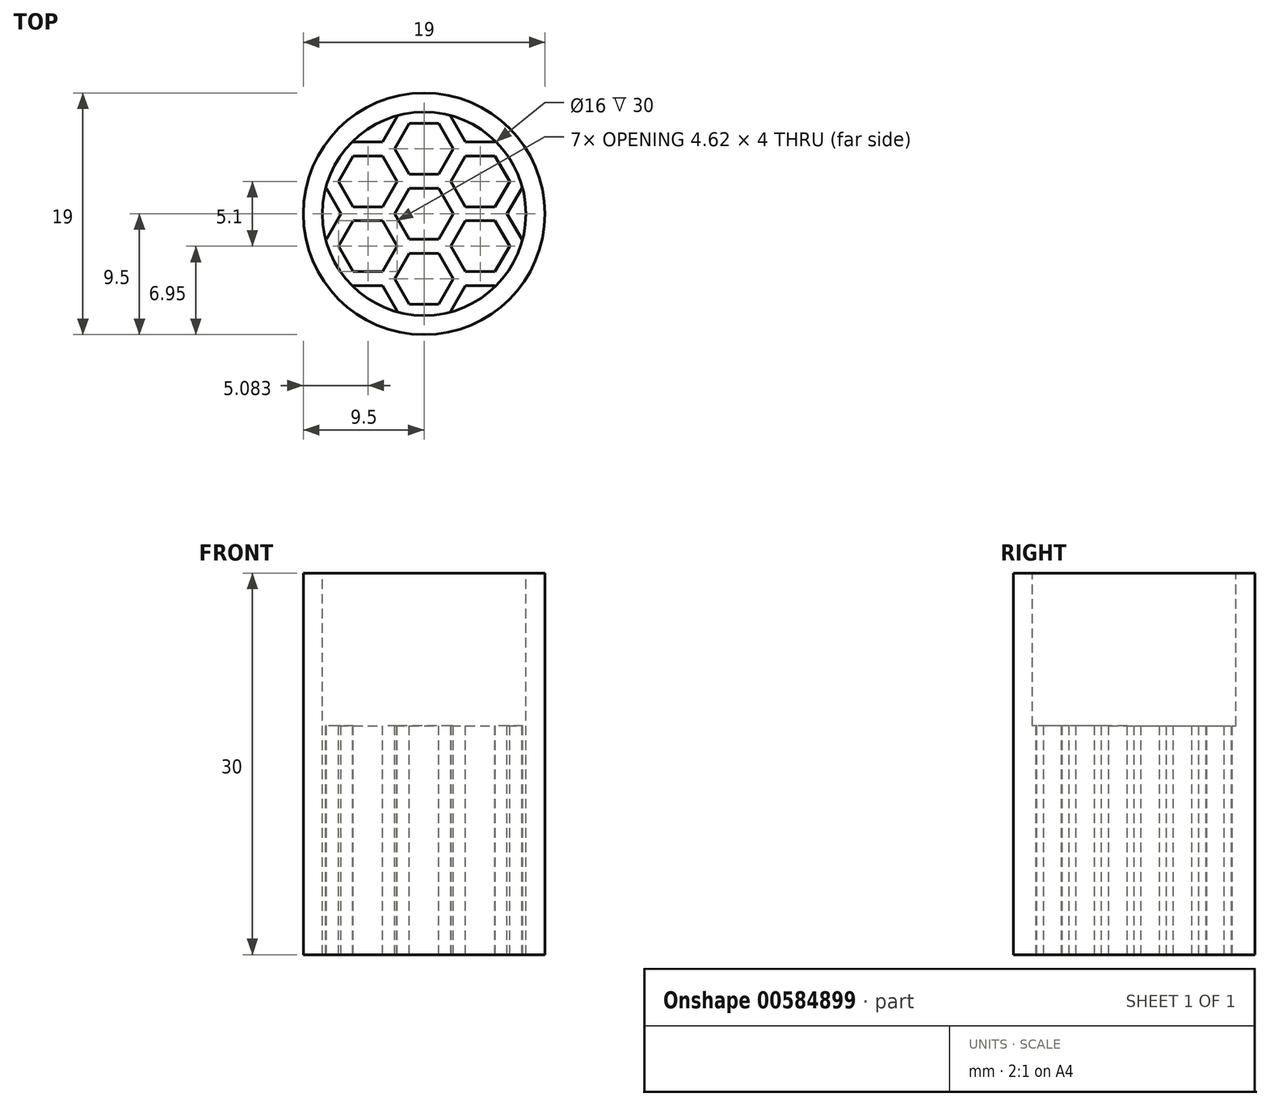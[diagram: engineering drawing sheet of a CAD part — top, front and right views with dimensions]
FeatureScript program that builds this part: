
annotation { "Feature Type Name" : "Feature", "Feature Type Description" : "" }
export const myFeature = defineFeature(function(context is Context, id is Id, definition is map)
    precondition{}
    {
        {
            var Q0;
            Q0=qCreatedBy(makeId("Top.planeOp"),FACE);
            var sketch = newSketch(context, id + "F0", { "sketchPlane" : qUnion([Q0])});
            skCircle(sketch, "E0", {"center": v(0, 0) * mm, "radius": 9.5 * mm});
            skCircle(sketch, "E1", {"center": v(0, 0) * mm, "radius": 8 * mm});
            skCircle(sketch, "E2.cCircle", {"center": v(-10.76, 15.35) * mm, "radius": 2 * mm, "construction": true});
            skLineSegment(sketch, "E2.0", {"start": v(-8.45, 15.35) * mm, "end": v(-9.6, 13.35) * mm});
            skLineSegment(sketch, "E2.1", {"start": v(-9.6, 13.35) * mm, "end": v(-11.91, 13.35) * mm});
            skLineSegment(sketch, "E2.2", {"start": v(-11.91, 13.35) * mm, "end": v(-13.07, 15.35) * mm});
            skLineSegment(sketch, "E2.3", {"start": v(-13.07, 15.35) * mm, "end": v(-11.91, 17.35) * mm});
            skLineSegment(sketch, "E2.4", {"start": v(-11.91, 17.35) * mm, "end": v(-9.6, 17.35) * mm});
            skLineSegment(sketch, "E2.5", {"start": v(-9.6, 17.35) * mm, "end": v(-8.45, 15.35) * mm});
            skPoint(sketch, "E2.0.midPoint", {"position": v(-9.02, 14.35) * mm});
            skCircle(sketch, "E3.cCircle", {"center": v(-10.76, 15.35) * mm, "radius": 2.55 * mm, "construction": true});
            skLineSegment(sketch, "E3.0", {"start": v(-7.81, 15.35) * mm, "end": v(-9.28, 12.8) * mm});
            skLineSegment(sketch, "E3.1", {"start": v(-9.28, 12.8) * mm, "end": v(-12.23, 12.8) * mm});
            skLineSegment(sketch, "E3.2", {"start": v(-12.23, 12.8) * mm, "end": v(-13.7, 15.35) * mm});
            skLineSegment(sketch, "E3.3", {"start": v(-13.7, 15.35) * mm, "end": v(-12.23, 17.9) * mm});
            skLineSegment(sketch, "E3.4", {"start": v(-12.23, 17.9) * mm, "end": v(-9.28, 17.9) * mm});
            skLineSegment(sketch, "E3.5", {"start": v(-9.28, 17.9) * mm, "end": v(-7.81, 15.35) * mm});
            skPoint(sketch, "E3.0.midPoint", {"position": v(-8.55, 14.07) * mm});
            skCircle(sketch, "E4.cCircle", {"center": v(0, 0) * mm, "radius": 2 * mm, "construction": true});
            skLineSegment(sketch, "E4.0", {"start": v(2.3, 0) * mm, "end": v(1.15, -2) * mm});
            skLineSegment(sketch, "E4.1", {"start": v(1.15, -2) * mm, "end": v(-1.15, -2) * mm});
            skLineSegment(sketch, "E4.2", {"start": v(-1.15, -2) * mm, "end": v(-2.3, 0) * mm});
            skLineSegment(sketch, "E4.3", {"start": v(-2.3, 0) * mm, "end": v(-1.15, 2) * mm});
            skLineSegment(sketch, "E4.4", {"start": v(-1.15, 2) * mm, "end": v(1.15, 2) * mm});
            skLineSegment(sketch, "E4.5", {"start": v(1.15, 2) * mm, "end": v(2.3, 0) * mm});
            skPoint(sketch, "E4.0.midPoint", {"position": v(1.73, -1) * mm});
            skCircle(sketch, "E5.cCircle", {"center": v(0, 0) * mm, "radius": 2.55 * mm, "construction": true});
            skLineSegment(sketch, "E5.0", {"start": v(2.94, 0) * mm, "end": v(1.47, -2.55) * mm});
            skLineSegment(sketch, "E5.1", {"start": v(1.47, -2.55) * mm, "end": v(-1.47, -2.55) * mm});
            skLineSegment(sketch, "E5.2", {"start": v(-1.47, -2.55) * mm, "end": v(-2.94, 0) * mm});
            skLineSegment(sketch, "E5.3", {"start": v(-2.94, 0) * mm, "end": v(-1.47, 2.55) * mm});
            skLineSegment(sketch, "E5.4", {"start": v(-1.47, 2.55) * mm, "end": v(1.47, 2.55) * mm});
            skLineSegment(sketch, "E5.5", {"start": v(1.47, 2.55) * mm, "end": v(2.94, 0) * mm});
            skPoint(sketch, "E5.0.midPoint", {"position": v(2.2, -1.28) * mm});
            skCircle(sketch, "E6.cCircle", {"center": v(4.42, 2.55) * mm, "radius": 2 * mm, "construction": true});
            skLineSegment(sketch, "E6.0", {"start": v(6.73, 2.55) * mm, "end": v(5.57, 0.55) * mm});
            skLineSegment(sketch, "E6.1", {"start": v(5.57, 0.55) * mm, "end": v(3.26, 0.55) * mm});
            skLineSegment(sketch, "E6.2", {"start": v(3.26, 0.55) * mm, "end": v(2.1, 2.55) * mm});
            skLineSegment(sketch, "E6.3", {"start": v(2.1, 2.55) * mm, "end": v(3.26, 4.55) * mm});
            skLineSegment(sketch, "E6.4", {"start": v(3.26, 4.55) * mm, "end": v(5.57, 4.55) * mm});
            skLineSegment(sketch, "E6.5", {"start": v(5.57, 4.55) * mm, "end": v(6.73, 2.55) * mm});
            skPoint(sketch, "E6.0.midPoint", {"position": v(6.15, 1.55) * mm});
            skCircle(sketch, "E7.cCircle", {"center": v(4.42, 2.55) * mm, "radius": 2.55 * mm, "construction": true});
            skLineSegment(sketch, "E7.0", {"start": v(7.36, 2.55) * mm, "end": v(5.89, 0) * mm});
            skLineSegment(sketch, "E7.1", {"start": v(5.89, 0) * mm, "end": v(2.94, 0) * mm});
            skLineSegment(sketch, "E7.2", {"start": v(2.94, 0) * mm, "end": v(1.47, 2.55) * mm});
            skLineSegment(sketch, "E7.3", {"start": v(1.47, 2.55) * mm, "end": v(2.94, 5.1) * mm});
            skLineSegment(sketch, "E7.4", {"start": v(2.94, 5.1) * mm, "end": v(5.89, 5.1) * mm});
            skLineSegment(sketch, "E7.5", {"start": v(5.89, 5.1) * mm, "end": v(7.36, 2.55) * mm});
            skPoint(sketch, "E7.0.midPoint", {"position": v(6.62, 1.27) * mm});
            skCircle(sketch, "E8.cCircle", {"center": v(0, 5.1) * mm, "radius": 2 * mm, "construction": true});
            skLineSegment(sketch, "E8.0", {"start": v(2.3, 5.1) * mm, "end": v(1.15, 3.1) * mm});
            skLineSegment(sketch, "E8.1", {"start": v(1.15, 3.1) * mm, "end": v(-1.15, 3.1) * mm});
            skLineSegment(sketch, "E8.2", {"start": v(-1.15, 3.1) * mm, "end": v(-2.3, 5.1) * mm});
            skLineSegment(sketch, "E8.3", {"start": v(-2.3, 5.1) * mm, "end": v(-1.15, 7.1) * mm});
            skLineSegment(sketch, "E8.4", {"start": v(-1.15, 7.1) * mm, "end": v(1.15, 7.1) * mm});
            skLineSegment(sketch, "E8.5", {"start": v(1.15, 7.1) * mm, "end": v(2.3, 5.1) * mm});
            skPoint(sketch, "E8.0.midPoint", {"position": v(1.73, 4.1) * mm});
            skCircle(sketch, "E9.cCircle", {"center": v(0, 5.1) * mm, "radius": 2.55 * mm, "construction": true});
            skLineSegment(sketch, "E9.0", {"start": v(2.94, 5.1) * mm, "end": v(1.47, 2.55) * mm});
            skLineSegment(sketch, "E9.1", {"start": v(1.47, 2.55) * mm, "end": v(-1.47, 2.55) * mm});
            skLineSegment(sketch, "E9.2", {"start": v(-1.47, 2.55) * mm, "end": v(-2.94, 5.1) * mm});
            skLineSegment(sketch, "E9.3", {"start": v(-2.94, 5.1) * mm, "end": v(-1.47, 7.65) * mm});
            skLineSegment(sketch, "E9.4", {"start": v(-1.47, 7.65) * mm, "end": v(1.47, 7.65) * mm});
            skLineSegment(sketch, "E9.5", {"start": v(1.47, 7.65) * mm, "end": v(2.94, 5.1) * mm});
            skPoint(sketch, "E9.0.midPoint", {"position": v(2.2, 3.82) * mm});
            skCircle(sketch, "E10.cCircle", {"center": v(4.42, 7.65) * mm, "radius": 2 * mm, "construction": true});
            skLineSegment(sketch, "E10.0", {"start": v(6.73, 7.65) * mm, "end": v(5.57, 5.65) * mm});
            skLineSegment(sketch, "E10.1", {"start": v(5.57, 5.65) * mm, "end": v(3.26, 5.65) * mm});
            skLineSegment(sketch, "E10.2", {"start": v(3.26, 5.65) * mm, "end": v(2.1, 7.65) * mm});
            skLineSegment(sketch, "E10.3", {"start": v(2.1, 7.65) * mm, "end": v(3.26, 9.65) * mm});
            skLineSegment(sketch, "E10.4", {"start": v(3.26, 9.65) * mm, "end": v(5.57, 9.65) * mm});
            skLineSegment(sketch, "E10.5", {"start": v(5.57, 9.65) * mm, "end": v(6.73, 7.65) * mm});
            skPoint(sketch, "E10.0.midPoint", {"position": v(6.15, 6.65) * mm});
            skCircle(sketch, "E11.cCircle", {"center": v(4.42, 7.65) * mm, "radius": 2.55 * mm, "construction": true});
            skLineSegment(sketch, "E11.0", {"start": v(7.36, 7.65) * mm, "end": v(5.89, 5.1) * mm});
            skLineSegment(sketch, "E11.1", {"start": v(5.89, 5.1) * mm, "end": v(2.94, 5.1) * mm});
            skLineSegment(sketch, "E11.2", {"start": v(2.94, 5.1) * mm, "end": v(1.47, 7.65) * mm});
            skLineSegment(sketch, "E11.3", {"start": v(1.47, 7.65) * mm, "end": v(2.94, 10.2) * mm});
            skLineSegment(sketch, "E11.4", {"start": v(2.94, 10.2) * mm, "end": v(5.89, 10.2) * mm});
            skLineSegment(sketch, "E11.5", {"start": v(5.89, 10.2) * mm, "end": v(7.36, 7.65) * mm});
            skPoint(sketch, "E11.0.midPoint", {"position": v(6.62, 6.37) * mm});
            skCircle(sketch, "E12.cCircle", {"center": v(4.42, -2.55) * mm, "radius": 2 * mm, "construction": true});
            skLineSegment(sketch, "E12.0", {"start": v(3.26, -4.55) * mm, "end": v(2.1, -2.55) * mm});
            skLineSegment(sketch, "E12.1", {"start": v(2.1, -2.55) * mm, "end": v(3.26, -0.55) * mm});
            skLineSegment(sketch, "E12.2", {"start": v(3.26, -0.55) * mm, "end": v(5.57, -0.55) * mm});
            skLineSegment(sketch, "E12.3", {"start": v(5.57, -0.55) * mm, "end": v(6.73, -2.55) * mm});
            skLineSegment(sketch, "E12.4", {"start": v(6.73, -2.55) * mm, "end": v(5.57, -4.55) * mm});
            skLineSegment(sketch, "E12.5", {"start": v(5.57, -4.55) * mm, "end": v(3.26, -4.55) * mm});
            skPoint(sketch, "E12.0.midPoint", {"position": v(2.68, -3.55) * mm});
            skCircle(sketch, "E13.cCircle", {"center": v(4.42, -2.55) * mm, "radius": 2.55 * mm, "construction": true});
            skLineSegment(sketch, "E13.0", {"start": v(2.94, -5.1) * mm, "end": v(1.47, -2.55) * mm});
            skLineSegment(sketch, "E13.1", {"start": v(1.47, -2.55) * mm, "end": v(2.94, 0) * mm});
            skLineSegment(sketch, "E13.2", {"start": v(2.94, 0) * mm, "end": v(5.89, 0) * mm});
            skLineSegment(sketch, "E13.3", {"start": v(5.89, 0) * mm, "end": v(7.36, -2.55) * mm});
            skLineSegment(sketch, "E13.4", {"start": v(7.36, -2.55) * mm, "end": v(5.89, -5.1) * mm});
            skLineSegment(sketch, "E13.5", {"start": v(5.89, -5.1) * mm, "end": v(2.94, -5.1) * mm});
            skPoint(sketch, "E13.0.midPoint", {"position": v(2.2, -3.82) * mm});
            skCircle(sketch, "E14.cCircle", {"center": v(8.83, 0) * mm, "radius": 2 * mm, "construction": true});
            skLineSegment(sketch, "E14.0", {"start": v(11.14, 0) * mm, "end": v(9.99, -2) * mm});
            skLineSegment(sketch, "E14.1", {"start": v(9.99, -2) * mm, "end": v(7.68, -2) * mm});
            skLineSegment(sketch, "E14.2", {"start": v(7.68, -2) * mm, "end": v(6.52, 0) * mm});
            skLineSegment(sketch, "E14.3", {"start": v(6.52, 0) * mm, "end": v(7.68, 2) * mm});
            skLineSegment(sketch, "E14.4", {"start": v(7.68, 2) * mm, "end": v(9.99, 2) * mm});
            skLineSegment(sketch, "E14.5", {"start": v(9.99, 2) * mm, "end": v(11.14, 0) * mm});
            skPoint(sketch, "E14.0.midPoint", {"position": v(10.57, -1) * mm});
            skCircle(sketch, "E15.cCircle", {"center": v(8.83, 0) * mm, "radius": 2.55 * mm, "construction": true});
            skLineSegment(sketch, "E15.0", {"start": v(11.78, 0) * mm, "end": v(10.3, -2.55) * mm});
            skLineSegment(sketch, "E15.1", {"start": v(10.3, -2.55) * mm, "end": v(7.36, -2.55) * mm});
            skLineSegment(sketch, "E15.2", {"start": v(7.36, -2.55) * mm, "end": v(5.89, 0) * mm});
            skLineSegment(sketch, "E15.3", {"start": v(5.89, 0) * mm, "end": v(7.36, 2.55) * mm});
            skLineSegment(sketch, "E15.4", {"start": v(7.36, 2.55) * mm, "end": v(10.3, 2.55) * mm});
            skLineSegment(sketch, "E15.5", {"start": v(10.3, 2.55) * mm, "end": v(11.78, 0) * mm});
            skPoint(sketch, "E15.0.midPoint", {"position": v(11.04, -1.28) * mm});
            skCircle(sketch, "E16.cCircle", {"center": v(0, -5.1) * mm, "radius": 2 * mm, "construction": true});
            skLineSegment(sketch, "E16.0", {"start": v(-1.15, -7.1) * mm, "end": v(-2.3, -5.1) * mm});
            skLineSegment(sketch, "E16.1", {"start": v(-2.3, -5.1) * mm, "end": v(-1.15, -3.1) * mm});
            skLineSegment(sketch, "E16.2", {"start": v(-1.15, -3.1) * mm, "end": v(1.15, -3.1) * mm});
            skLineSegment(sketch, "E16.3", {"start": v(1.15, -3.1) * mm, "end": v(2.3, -5.1) * mm});
            skLineSegment(sketch, "E16.4", {"start": v(2.3, -5.1) * mm, "end": v(1.15, -7.1) * mm});
            skLineSegment(sketch, "E16.5", {"start": v(1.15, -7.1) * mm, "end": v(-1.15, -7.1) * mm});
            skPoint(sketch, "E16.0.midPoint", {"position": v(-1.73, -6.1) * mm});
            skCircle(sketch, "E17.cCircle", {"center": v(0, -5.1) * mm, "radius": 2.55 * mm, "construction": true});
            skLineSegment(sketch, "E17.0", {"start": v(-1.47, -7.65) * mm, "end": v(-2.94, -5.1) * mm});
            skLineSegment(sketch, "E17.1", {"start": v(-2.94, -5.1) * mm, "end": v(-1.47, -2.55) * mm});
            skLineSegment(sketch, "E17.2", {"start": v(-1.47, -2.55) * mm, "end": v(1.47, -2.55) * mm});
            skLineSegment(sketch, "E17.3", {"start": v(1.47, -2.55) * mm, "end": v(2.94, -5.1) * mm});
            skLineSegment(sketch, "E17.4", {"start": v(2.94, -5.1) * mm, "end": v(1.47, -7.65) * mm});
            skLineSegment(sketch, "E17.5", {"start": v(1.47, -7.65) * mm, "end": v(-1.47, -7.65) * mm});
            skPoint(sketch, "E17.0.midPoint", {"position": v(-2.21, -6.37) * mm});
            skCircle(sketch, "E18.cCircle", {"center": v(4.42, -7.65) * mm, "radius": 2 * mm, "construction": true});
            skLineSegment(sketch, "E18.0", {"start": v(3.26, -9.65) * mm, "end": v(2.1, -7.65) * mm});
            skLineSegment(sketch, "E18.1", {"start": v(2.1, -7.65) * mm, "end": v(3.26, -5.65) * mm});
            skLineSegment(sketch, "E18.2", {"start": v(3.26, -5.65) * mm, "end": v(5.57, -5.65) * mm});
            skLineSegment(sketch, "E18.3", {"start": v(5.57, -5.65) * mm, "end": v(6.73, -7.65) * mm});
            skLineSegment(sketch, "E18.4", {"start": v(6.73, -7.65) * mm, "end": v(5.57, -9.65) * mm});
            skLineSegment(sketch, "E18.5", {"start": v(5.57, -9.65) * mm, "end": v(3.26, -9.65) * mm});
            skPoint(sketch, "E18.0.midPoint", {"position": v(2.68, -8.65) * mm});
            skCircle(sketch, "E19.cCircle", {"center": v(4.42, -7.65) * mm, "radius": 2.55 * mm, "construction": true});
            skLineSegment(sketch, "E19.0", {"start": v(2.94, -10.2) * mm, "end": v(1.47, -7.65) * mm});
            skLineSegment(sketch, "E19.1", {"start": v(1.47, -7.65) * mm, "end": v(2.94, -5.1) * mm});
            skLineSegment(sketch, "E19.2", {"start": v(2.94, -5.1) * mm, "end": v(5.89, -5.1) * mm});
            skLineSegment(sketch, "E19.3", {"start": v(5.89, -5.1) * mm, "end": v(7.36, -7.65) * mm});
            skLineSegment(sketch, "E19.4", {"start": v(7.36, -7.65) * mm, "end": v(5.89, -10.2) * mm});
            skLineSegment(sketch, "E19.5", {"start": v(5.89, -10.2) * mm, "end": v(2.94, -10.2) * mm});
            skPoint(sketch, "E19.0.midPoint", {"position": v(2.2, -8.92) * mm});
            skCircle(sketch, "E20.cCircle", {"center": v(-4.42, -2.55) * mm, "radius": 2 * mm, "construction": true});
            skLineSegment(sketch, "E20.0", {"start": v(-3.26, -0.55) * mm, "end": v(-2.1, -2.55) * mm});
            skLineSegment(sketch, "E20.1", {"start": v(-2.1, -2.55) * mm, "end": v(-3.26, -4.55) * mm});
            skLineSegment(sketch, "E20.2", {"start": v(-3.26, -4.55) * mm, "end": v(-5.57, -4.55) * mm});
            skLineSegment(sketch, "E20.3", {"start": v(-5.57, -4.55) * mm, "end": v(-6.73, -2.55) * mm});
            skLineSegment(sketch, "E20.4", {"start": v(-6.73, -2.55) * mm, "end": v(-5.57, -0.55) * mm});
            skLineSegment(sketch, "E20.5", {"start": v(-5.57, -0.55) * mm, "end": v(-3.26, -0.55) * mm});
            skPoint(sketch, "E20.0.midPoint", {"position": v(-2.68, -1.55) * mm});
            skCircle(sketch, "E21.cCircle", {"center": v(-4.42, -2.55) * mm, "radius": 2.55 * mm, "construction": true});
            skLineSegment(sketch, "E21.0", {"start": v(-2.94, 0) * mm, "end": v(-1.47, -2.55) * mm});
            skLineSegment(sketch, "E21.1", {"start": v(-1.47, -2.55) * mm, "end": v(-2.94, -5.1) * mm});
            skLineSegment(sketch, "E21.2", {"start": v(-2.94, -5.1) * mm, "end": v(-5.89, -5.1) * mm});
            skLineSegment(sketch, "E21.3", {"start": v(-5.89, -5.1) * mm, "end": v(-7.36, -2.55) * mm});
            skLineSegment(sketch, "E21.4", {"start": v(-7.36, -2.55) * mm, "end": v(-5.89, 0) * mm});
            skLineSegment(sketch, "E21.5", {"start": v(-5.89, 0) * mm, "end": v(-2.94, 0) * mm});
            skPoint(sketch, "E21.0.midPoint", {"position": v(-2.2, -1.28) * mm});
            skCircle(sketch, "E22.cCircle", {"center": v(-4.42, -7.65) * mm, "radius": 2 * mm, "construction": true});
            skLineSegment(sketch, "E22.0", {"start": v(-6.73, -7.65) * mm, "end": v(-5.57, -5.65) * mm});
            skLineSegment(sketch, "E22.1", {"start": v(-5.57, -5.65) * mm, "end": v(-3.26, -5.65) * mm});
            skLineSegment(sketch, "E22.2", {"start": v(-3.26, -5.65) * mm, "end": v(-2.1, -7.65) * mm});
            skLineSegment(sketch, "E22.3", {"start": v(-2.1, -7.65) * mm, "end": v(-3.26, -9.65) * mm});
            skLineSegment(sketch, "E22.4", {"start": v(-3.26, -9.65) * mm, "end": v(-5.57, -9.65) * mm});
            skLineSegment(sketch, "E22.5", {"start": v(-5.57, -9.65) * mm, "end": v(-6.73, -7.65) * mm});
            skPoint(sketch, "E22.0.midPoint", {"position": v(-6.15, -6.65) * mm});
            skCircle(sketch, "E23.cCircle", {"center": v(-4.42, -7.65) * mm, "radius": 2.55 * mm, "construction": true});
            skLineSegment(sketch, "E23.0", {"start": v(-7.36, -7.65) * mm, "end": v(-5.89, -5.1) * mm});
            skLineSegment(sketch, "E23.1", {"start": v(-5.89, -5.1) * mm, "end": v(-2.94, -5.1) * mm});
            skLineSegment(sketch, "E23.2", {"start": v(-2.94, -5.1) * mm, "end": v(-1.47, -7.65) * mm});
            skLineSegment(sketch, "E23.3", {"start": v(-1.47, -7.65) * mm, "end": v(-2.94, -10.2) * mm});
            skLineSegment(sketch, "E23.4", {"start": v(-2.94, -10.2) * mm, "end": v(-5.89, -10.2) * mm});
            skLineSegment(sketch, "E23.5", {"start": v(-5.89, -10.2) * mm, "end": v(-7.36, -7.65) * mm});
            skPoint(sketch, "E23.0.midPoint", {"position": v(-6.62, -6.37) * mm});
            skCircle(sketch, "E24.cCircle", {"center": v(-8.83, 0) * mm, "radius": 2 * mm, "construction": true});
            skLineSegment(sketch, "E24.0", {"start": v(-7.68, 2) * mm, "end": v(-6.52, 0) * mm});
            skLineSegment(sketch, "E24.1", {"start": v(-6.52, 0) * mm, "end": v(-7.68, -2) * mm});
            skLineSegment(sketch, "E24.2", {"start": v(-7.68, -2) * mm, "end": v(-9.99, -2) * mm});
            skLineSegment(sketch, "E24.3", {"start": v(-9.99, -2) * mm, "end": v(-11.14, 0) * mm});
            skLineSegment(sketch, "E24.4", {"start": v(-11.14, 0) * mm, "end": v(-9.99, 2) * mm});
            skLineSegment(sketch, "E24.5", {"start": v(-9.99, 2) * mm, "end": v(-7.68, 2) * mm});
            skPoint(sketch, "E24.0.midPoint", {"position": v(-7.1, 1) * mm});
            skCircle(sketch, "E25.cCircle", {"center": v(-8.83, 0) * mm, "radius": 2.55 * mm, "construction": true});
            skLineSegment(sketch, "E25.0", {"start": v(-7.36, 2.55) * mm, "end": v(-5.89, 0) * mm});
            skLineSegment(sketch, "E25.1", {"start": v(-5.89, 0) * mm, "end": v(-7.36, -2.55) * mm});
            skLineSegment(sketch, "E25.2", {"start": v(-7.36, -2.55) * mm, "end": v(-10.3, -2.55) * mm});
            skLineSegment(sketch, "E25.3", {"start": v(-10.3, -2.55) * mm, "end": v(-11.78, 0) * mm});
            skLineSegment(sketch, "E25.4", {"start": v(-11.78, 0) * mm, "end": v(-10.3, 2.55) * mm});
            skLineSegment(sketch, "E25.5", {"start": v(-10.3, 2.55) * mm, "end": v(-7.36, 2.55) * mm});
            skPoint(sketch, "E25.0.midPoint", {"position": v(-6.62, 1.27) * mm});
            skCircle(sketch, "E26.cCircle", {"center": v(-4.42, 2.55) * mm, "radius": 2 * mm, "construction": true});
            skLineSegment(sketch, "E26.0", {"start": v(-2.1, 2.55) * mm, "end": v(-3.26, 0.55) * mm});
            skLineSegment(sketch, "E26.1", {"start": v(-3.26, 0.55) * mm, "end": v(-5.57, 0.55) * mm});
            skLineSegment(sketch, "E26.2", {"start": v(-5.57, 0.55) * mm, "end": v(-6.73, 2.55) * mm});
            skLineSegment(sketch, "E26.3", {"start": v(-6.73, 2.55) * mm, "end": v(-5.57, 4.55) * mm});
            skLineSegment(sketch, "E26.4", {"start": v(-5.57, 4.55) * mm, "end": v(-3.26, 4.55) * mm});
            skLineSegment(sketch, "E26.5", {"start": v(-3.26, 4.55) * mm, "end": v(-2.1, 2.55) * mm});
            skPoint(sketch, "E26.0.midPoint", {"position": v(-2.68, 1.55) * mm});
            skCircle(sketch, "E27.cCircle", {"center": v(-4.42, 2.55) * mm, "radius": 2.55 * mm, "construction": true});
            skLineSegment(sketch, "E27.0", {"start": v(-1.47, 2.55) * mm, "end": v(-2.94, 0) * mm});
            skLineSegment(sketch, "E27.1", {"start": v(-2.94, 0) * mm, "end": v(-5.89, 0) * mm});
            skLineSegment(sketch, "E27.2", {"start": v(-5.89, 0) * mm, "end": v(-7.36, 2.55) * mm});
            skLineSegment(sketch, "E27.3", {"start": v(-7.36, 2.55) * mm, "end": v(-5.89, 5.1) * mm});
            skLineSegment(sketch, "E27.4", {"start": v(-5.89, 5.1) * mm, "end": v(-2.94, 5.1) * mm});
            skLineSegment(sketch, "E27.5", {"start": v(-2.94, 5.1) * mm, "end": v(-1.47, 2.55) * mm});
            skPoint(sketch, "E27.0.midPoint", {"position": v(-2.21, 1.27) * mm});
            skCircle(sketch, "E28.cCircle", {"center": v(-4.42, 7.65) * mm, "radius": 2 * mm, "construction": true});
            skLineSegment(sketch, "E28.0", {"start": v(-3.26, 9.65) * mm, "end": v(-2.1, 7.65) * mm});
            skLineSegment(sketch, "E28.1", {"start": v(-2.1, 7.65) * mm, "end": v(-3.26, 5.65) * mm});
            skLineSegment(sketch, "E28.2", {"start": v(-3.26, 5.65) * mm, "end": v(-5.57, 5.65) * mm});
            skLineSegment(sketch, "E28.3", {"start": v(-5.57, 5.65) * mm, "end": v(-6.73, 7.65) * mm});
            skLineSegment(sketch, "E28.4", {"start": v(-6.73, 7.65) * mm, "end": v(-5.57, 9.65) * mm});
            skLineSegment(sketch, "E28.5", {"start": v(-5.57, 9.65) * mm, "end": v(-3.26, 9.65) * mm});
            skPoint(sketch, "E28.0.midPoint", {"position": v(-2.68, 8.65) * mm});
            skCircle(sketch, "E29.cCircle", {"center": v(-4.42, 7.65) * mm, "radius": 2.55 * mm, "construction": true});
            skLineSegment(sketch, "E29.0", {"start": v(-2.94, 10.2) * mm, "end": v(-1.47, 7.65) * mm});
            skLineSegment(sketch, "E29.1", {"start": v(-1.47, 7.65) * mm, "end": v(-2.94, 5.1) * mm});
            skLineSegment(sketch, "E29.2", {"start": v(-2.94, 5.1) * mm, "end": v(-5.89, 5.1) * mm});
            skLineSegment(sketch, "E29.3", {"start": v(-5.89, 5.1) * mm, "end": v(-7.36, 7.65) * mm});
            skLineSegment(sketch, "E29.4", {"start": v(-7.36, 7.65) * mm, "end": v(-5.89, 10.2) * mm});
            skLineSegment(sketch, "E29.5", {"start": v(-5.89, 10.2) * mm, "end": v(-2.94, 10.2) * mm});
            skPoint(sketch, "E29.0.midPoint", {"position": v(-2.2, 8.92) * mm});
            skSolve(sketch);
        }
        {
            var Q0;
            {var subQ0=sQuery(id+"F0.wireOp",EDGE,"E29.3");var subQ1=sQuery(id+"F0.wireOp",EDGE,"E0");var subQ2=makeQuery(id+"F0.imprint","INTERSECT",VERTEX,{"derivedFrom":[subQ1,subQ0]});Q0=makeQuery(id+"F0.imprint","IMPRINT",FACE,{"disambiguationData":[TD([[makeQuery(id+"F0.imprint","IMPRINT",EDGE,{"disambiguationData":[TD([[subQ2,-1.0]])],"derivedFrom":subQ1}),1.0]])]});}
            var Q1;
            {var subQ0=sQuery(id+"F0.wireOp",EDGE,"E25.5");var subQ1=sQuery(id+"F0.wireOp",EDGE,"E0");var subQ2=makeQuery(id+"F0.imprint","INTERSECT",VERTEX,{"derivedFrom":[subQ1,subQ0]});Q1=makeQuery(id+"F0.imprint","IMPRINT",FACE,{"disambiguationData":[TD([[makeQuery(id+"F0.imprint","IMPRINT",EDGE,{"disambiguationData":[TD([[subQ2,-1.0]])],"derivedFrom":subQ1}),1.0]])]});}
            var Q2;
            {var subQ0=sQuery(id+"F0.wireOp",EDGE,"E24.5");var subQ1=sQuery(id+"F0.wireOp",EDGE,"E0");var subQ2=makeQuery(id+"F0.imprint","INTERSECT",VERTEX,{"derivedFrom":[subQ1,subQ0]});Q2=makeQuery(id+"F0.imprint","IMPRINT",FACE,{"disambiguationData":[TD([[makeQuery(id+"F0.imprint","IMPRINT",EDGE,{"disambiguationData":[TD([[subQ2,-1.0]])],"derivedFrom":subQ1}),1.0]])]});}
            var Q3;
            {var subQ0=sQuery(id+"F0.wireOp",EDGE,"E25.2");var subQ1=sQuery(id+"F0.wireOp",EDGE,"E0");var subQ2=makeQuery(id+"F0.imprint","INTERSECT",VERTEX,{"derivedFrom":[subQ1,subQ0]});Q3=makeQuery(id+"F0.imprint","IMPRINT",FACE,{"disambiguationData":[TD([[makeQuery(id+"F0.imprint","IMPRINT",EDGE,{"disambiguationData":[TD([[subQ2,1.0]])],"derivedFrom":subQ1}),1.0]])]});}
            var Q4;
            {var subQ0=sQuery(id+"F0.wireOp",EDGE,"E25.2");var subQ1=sQuery(id+"F0.wireOp",EDGE,"E0");var subQ2=makeQuery(id+"F0.imprint","INTERSECT",VERTEX,{"derivedFrom":[subQ1,subQ0]});Q4=makeQuery(id+"F0.imprint","IMPRINT",FACE,{"disambiguationData":[TD([[makeQuery(id+"F0.imprint","IMPRINT",EDGE,{"disambiguationData":[TD([[subQ2,-1.0]])],"derivedFrom":subQ1}),1.0]])]});}
            var Q5;
            {var subQ0=sQuery(id+"F0.wireOp",EDGE,"E23.0");var subQ1=sQuery(id+"F0.wireOp",EDGE,"E0");var subQ2=makeQuery(id+"F0.imprint","INTERSECT",VERTEX,{"derivedFrom":[subQ1,subQ0]});Q5=makeQuery(id+"F0.imprint","IMPRINT",FACE,{"disambiguationData":[TD([[makeQuery(id+"F0.imprint","IMPRINT",EDGE,{"disambiguationData":[TD([[subQ2,-1.0]])],"derivedFrom":subQ1}),1.0]])]});}
            var Q6;
            {var subQ0=sQuery(id+"F0.wireOp",EDGE,"E22.0");var subQ1=sQuery(id+"F0.wireOp",EDGE,"E0");var subQ2=makeQuery(id+"F0.imprint","INTERSECT",VERTEX,{"derivedFrom":[subQ1,subQ0]});Q6=makeQuery(id+"F0.imprint","IMPRINT",FACE,{"disambiguationData":[TD([[makeQuery(id+"F0.imprint","IMPRINT",EDGE,{"disambiguationData":[TD([[subQ2,-1.0]])],"derivedFrom":subQ1}),1.0]])]});}
            var Q7;
            {var subQ0=sQuery(id+"F0.wireOp",EDGE,"E23.3");var subQ1=sQuery(id+"F0.wireOp",EDGE,"E0");var subQ2=makeQuery(id+"F0.imprint","INTERSECT",VERTEX,{"derivedFrom":[subQ1,subQ0]});Q7=makeQuery(id+"F0.imprint","IMPRINT",FACE,{"disambiguationData":[TD([[makeQuery(id+"F0.imprint","IMPRINT",EDGE,{"disambiguationData":[TD([[subQ2,1.0]])],"derivedFrom":subQ1}),1.0]])]});}
            var Q8;
            {var subQ0=sQuery(id+"F0.wireOp",EDGE,"E23.3");var subQ1=sQuery(id+"F0.wireOp",EDGE,"E0");var subQ2=makeQuery(id+"F0.imprint","INTERSECT",VERTEX,{"derivedFrom":[subQ1,subQ0]});Q8=makeQuery(id+"F0.imprint","IMPRINT",FACE,{"disambiguationData":[TD([[makeQuery(id+"F0.imprint","IMPRINT",EDGE,{"disambiguationData":[TD([[subQ2,-1.0]])],"derivedFrom":subQ1}),1.0]])]});}
            var Q9;
            {var subQ0=sQuery(id+"F0.wireOp",EDGE,"E19.0");var subQ1=sQuery(id+"F0.wireOp",EDGE,"E0");var subQ2=makeQuery(id+"F0.imprint","INTERSECT",VERTEX,{"derivedFrom":[subQ1,subQ0]});Q9=makeQuery(id+"F0.imprint","IMPRINT",FACE,{"disambiguationData":[TD([[makeQuery(id+"F0.imprint","IMPRINT",EDGE,{"disambiguationData":[TD([[subQ2,-1.0]])],"derivedFrom":subQ1}),1.0]])]});}
            var Q10;
            {var subQ0=sQuery(id+"F0.wireOp",EDGE,"E18.0");var subQ1=sQuery(id+"F0.wireOp",EDGE,"E0");var subQ2=makeQuery(id+"F0.imprint","INTERSECT",VERTEX,{"derivedFrom":[subQ1,subQ0]});Q10=makeQuery(id+"F0.imprint","IMPRINT",FACE,{"disambiguationData":[TD([[makeQuery(id+"F0.imprint","IMPRINT",EDGE,{"disambiguationData":[TD([[subQ2,-1.0]])],"derivedFrom":subQ1}),1.0]])]});}
            var Q11;
            {var subQ0=sQuery(id+"F0.wireOp",EDGE,"E19.3");var subQ1=sQuery(id+"F0.wireOp",EDGE,"E0");var subQ2=makeQuery(id+"F0.imprint","INTERSECT",VERTEX,{"derivedFrom":[subQ1,subQ0]});Q11=makeQuery(id+"F0.imprint","IMPRINT",FACE,{"disambiguationData":[TD([[makeQuery(id+"F0.imprint","IMPRINT",EDGE,{"disambiguationData":[TD([[subQ2,1.0]])],"derivedFrom":subQ1}),1.0]])]});}
            var Q12;
            {var subQ0=sQuery(id+"F0.wireOp",EDGE,"E19.3");var subQ1=sQuery(id+"F0.wireOp",EDGE,"E0");var subQ2=makeQuery(id+"F0.imprint","INTERSECT",VERTEX,{"derivedFrom":[subQ1,subQ0]});Q12=makeQuery(id+"F0.imprint","IMPRINT",FACE,{"disambiguationData":[TD([[makeQuery(id+"F0.imprint","IMPRINT",EDGE,{"disambiguationData":[TD([[subQ2,-1.0]])],"derivedFrom":subQ1}),1.0]])]});}
            var Q13;
            {var subQ0=sQuery(id+"F0.wireOp",EDGE,"E15.1");var subQ1=sQuery(id+"F0.wireOp",EDGE,"E0");var subQ2=makeQuery(id+"F0.imprint","INTERSECT",VERTEX,{"derivedFrom":[subQ1,subQ0]});Q13=makeQuery(id+"F0.imprint","IMPRINT",FACE,{"disambiguationData":[TD([[makeQuery(id+"F0.imprint","IMPRINT",EDGE,{"disambiguationData":[TD([[subQ2,-1.0]])],"derivedFrom":subQ1}),1.0]])]});}
            var Q14;
            {var subQ0=sQuery(id+"F0.wireOp",EDGE,"E14.4");var subQ1=sQuery(id+"F0.wireOp",EDGE,"E0");var subQ2=makeQuery(id+"F0.imprint","INTERSECT",VERTEX,{"derivedFrom":[subQ1,subQ0]});Q14=makeQuery(id+"F0.imprint","IMPRINT",FACE,{"disambiguationData":[TD([[makeQuery(id+"F0.imprint","IMPRINT",EDGE,{"disambiguationData":[TD([[subQ2,1.0]])],"derivedFrom":subQ1}),1.0]])]});}
            var Q15;
            {var subQ0=sQuery(id+"F0.wireOp",EDGE,"E15.4");var subQ1=sQuery(id+"F0.wireOp",EDGE,"E0");var subQ2=makeQuery(id+"F0.imprint","INTERSECT",VERTEX,{"derivedFrom":[subQ1,subQ0]});Q15=makeQuery(id+"F0.imprint","IMPRINT",FACE,{"disambiguationData":[TD([[makeQuery(id+"F0.imprint","IMPRINT",EDGE,{"disambiguationData":[TD([[subQ2,1.0]])],"derivedFrom":subQ1}),1.0]])]});}
            var Q16;
            {var subQ0=sQuery(id+"F0.wireOp",EDGE,"E15.4");var subQ1=sQuery(id+"F0.wireOp",EDGE,"E0");var subQ2=makeQuery(id+"F0.imprint","INTERSECT",VERTEX,{"derivedFrom":[subQ1,subQ0]});Q16=makeQuery(id+"F0.imprint","IMPRINT",FACE,{"disambiguationData":[TD([[makeQuery(id+"F0.imprint","IMPRINT",EDGE,{"disambiguationData":[TD([[subQ2,-1.0]])],"derivedFrom":subQ1}),1.0]])]});}
            var Q17;
            {var subQ0=sQuery(id+"F0.wireOp",EDGE,"E11.0");var subQ1=sQuery(id+"F0.wireOp",EDGE,"E0");var subQ2=makeQuery(id+"F0.imprint","INTERSECT",VERTEX,{"derivedFrom":[subQ1,subQ0]});Q17=makeQuery(id+"F0.imprint","IMPRINT",FACE,{"disambiguationData":[TD([[makeQuery(id+"F0.imprint","IMPRINT",EDGE,{"disambiguationData":[TD([[subQ2,-1.0]])],"derivedFrom":subQ1}),1.0]])]});}
            var Q18;
            {var subQ0=sQuery(id+"F0.wireOp",EDGE,"E10.0");var subQ1=sQuery(id+"F0.wireOp",EDGE,"E0");var subQ2=makeQuery(id+"F0.imprint","INTERSECT",VERTEX,{"derivedFrom":[subQ1,subQ0]});Q18=makeQuery(id+"F0.imprint","IMPRINT",FACE,{"disambiguationData":[TD([[makeQuery(id+"F0.imprint","IMPRINT",EDGE,{"disambiguationData":[TD([[subQ2,-1.0]])],"derivedFrom":subQ1}),1.0]])]});}
            var Q19;
            {var subQ0=sQuery(id+"F0.wireOp",EDGE,"E11.3");var subQ1=sQuery(id+"F0.wireOp",EDGE,"E0");var subQ2=makeQuery(id+"F0.imprint","INTERSECT",VERTEX,{"derivedFrom":[subQ1,subQ0]});Q19=makeQuery(id+"F0.imprint","IMPRINT",FACE,{"disambiguationData":[TD([[makeQuery(id+"F0.imprint","IMPRINT",EDGE,{"disambiguationData":[TD([[subQ2,1.0]])],"derivedFrom":subQ1}),1.0]])]});}
            var Q20;
            {var subQ0=sQuery(id+"F0.wireOp",EDGE,"E11.3");var subQ1=sQuery(id+"F0.wireOp",EDGE,"E0");var subQ2=makeQuery(id+"F0.imprint","INTERSECT",VERTEX,{"derivedFrom":[subQ1,subQ0]});Q20=makeQuery(id+"F0.imprint","IMPRINT",FACE,{"disambiguationData":[TD([[makeQuery(id+"F0.imprint","IMPRINT",EDGE,{"disambiguationData":[TD([[subQ2,-1.0]])],"derivedFrom":subQ1}),1.0]])]});}
            var Q21;
            {var subQ0=sQuery(id+"F0.wireOp",EDGE,"E29.0");var subQ1=sQuery(id+"F0.wireOp",EDGE,"E0");var subQ2=makeQuery(id+"F0.imprint","INTERSECT",VERTEX,{"derivedFrom":[subQ1,subQ0]});Q21=makeQuery(id+"F0.imprint","IMPRINT",FACE,{"disambiguationData":[TD([[makeQuery(id+"F0.imprint","IMPRINT",EDGE,{"disambiguationData":[TD([[subQ2,-1.0]])],"derivedFrom":subQ1}),1.0]])]});}
            var Q22;
            {var subQ0=sQuery(id+"F0.wireOp",EDGE,"E28.0");var subQ1=sQuery(id+"F0.wireOp",EDGE,"E0");var subQ2=makeQuery(id+"F0.imprint","INTERSECT",VERTEX,{"derivedFrom":[subQ1,subQ0]});Q22=makeQuery(id+"F0.imprint","IMPRINT",FACE,{"disambiguationData":[TD([[makeQuery(id+"F0.imprint","IMPRINT",EDGE,{"disambiguationData":[TD([[subQ2,-1.0]])],"derivedFrom":subQ1}),1.0]])]});}
            var Q23;
            {var subQ0=sQuery(id+"F0.wireOp",EDGE,"E29.3");var subQ1=sQuery(id+"F0.wireOp",EDGE,"E0");var subQ2=makeQuery(id+"F0.imprint","INTERSECT",VERTEX,{"derivedFrom":[subQ1,subQ0]});Q23=makeQuery(id+"F0.imprint","IMPRINT",FACE,{"disambiguationData":[TD([[makeQuery(id+"F0.imprint","IMPRINT",EDGE,{"disambiguationData":[TD([[subQ2,1.0]])],"derivedFrom":subQ1}),1.0]])]});}
            var Q24;
            {var subQ5=sQuery(id+"F0.wireOp",EDGE,"E9.4");Q24=makeQuery(id+"F0.imprint","IMPRINT",FACE,{"disambiguationData":[TD([[makeQuery(id+"F0.imprint","IMPRINT",EDGE,{"derivedFrom":subQ5}),1.0]])]});}
            var Q25;
            {var subQ5=sQuery(id+"F0.wireOp",EDGE,"E27.3");Q25=makeQuery(id+"F0.imprint","IMPRINT",FACE,{"disambiguationData":[TD([[makeQuery(id+"F0.imprint","IMPRINT",EDGE,{"derivedFrom":subQ5}),1.0]])]});}
            var Q26;
            {var subQ5=sQuery(id+"F0.wireOp",EDGE,"E21.3");Q26=makeQuery(id+"F0.imprint","IMPRINT",FACE,{"disambiguationData":[TD([[makeQuery(id+"F0.imprint","IMPRINT",EDGE,{"derivedFrom":subQ5}),1.0]])]});}
            var Q27;
            {var subQ5=sQuery(id+"F0.wireOp",EDGE,"E17.5");Q27=makeQuery(id+"F0.imprint","IMPRINT",FACE,{"disambiguationData":[TD([[makeQuery(id+"F0.imprint","IMPRINT",EDGE,{"derivedFrom":subQ5}),1.0]])]});}
            var Q28;
            {var subQ5=sQuery(id+"F0.wireOp",EDGE,"E13.4");Q28=makeQuery(id+"F0.imprint","IMPRINT",FACE,{"disambiguationData":[TD([[makeQuery(id+"F0.imprint","IMPRINT",EDGE,{"derivedFrom":subQ5}),1.0]])]});}
            var Q29;
            {var subQ5=sQuery(id+"F0.wireOp",EDGE,"E7.5");Q29=makeQuery(id+"F0.imprint","IMPRINT",FACE,{"disambiguationData":[TD([[makeQuery(id+"F0.imprint","IMPRINT",EDGE,{"derivedFrom":subQ5}),1.0]])]});}
            var Q30;
            {var subQ0=sQuery(id+"F0.wireOp",EDGE,"E10.1");Q30=makeQuery(id+"F0.imprint","IMPRINT",FACE,{"disambiguationData":[TD([[makeQuery(id+"F0.imprint","IMPRINT",EDGE,{"derivedFrom":subQ0}),1.0]])]});}
            var Q31;
            {var subQ0=sQuery(id+"F0.wireOp",EDGE,"E28.1");Q31=makeQuery(id+"F0.imprint","IMPRINT",FACE,{"disambiguationData":[TD([[makeQuery(id+"F0.imprint","IMPRINT",EDGE,{"derivedFrom":subQ0}),1.0]])]});}
            var Q32;
            {var subQ0=sQuery(id+"F0.wireOp",EDGE,"E24.0");Q32=makeQuery(id+"F0.imprint","IMPRINT",FACE,{"disambiguationData":[TD([[makeQuery(id+"F0.imprint","IMPRINT",EDGE,{"derivedFrom":subQ0}),1.0]])]});}
            var Q33;
            {var subQ0=sQuery(id+"F0.wireOp",EDGE,"E14.2");Q33=makeQuery(id+"F0.imprint","IMPRINT",FACE,{"disambiguationData":[TD([[makeQuery(id+"F0.imprint","IMPRINT",EDGE,{"derivedFrom":subQ0}),1.0]])]});}
            var Q34;
            {var subQ0=sQuery(id+"F0.wireOp",EDGE,"E18.1");Q34=makeQuery(id+"F0.imprint","IMPRINT",FACE,{"disambiguationData":[TD([[makeQuery(id+"F0.imprint","IMPRINT",EDGE,{"derivedFrom":subQ0}),1.0]])]});}
            var Q35;
            {var subQ0=sQuery(id+"F0.wireOp",EDGE,"E22.1");Q35=makeQuery(id+"F0.imprint","IMPRINT",FACE,{"disambiguationData":[TD([[makeQuery(id+"F0.imprint","IMPRINT",EDGE,{"derivedFrom":subQ0}),1.0]])]});}
            var Q36;
            Q36=makeQuery(id+"F0.imprint","IMPRINT",FACE,{"disambiguationData":[TD([[makeQuery(id+"F0.imprint","IMPRINT",EDGE,{"derivedFrom":sQuery(id+"F0.wireOp",EDGE,"E20.0")}),1.0]])]});
            var Q37;
            Q37=makeQuery(id+"F0.imprint","IMPRINT",FACE,{"disambiguationData":[TD([[makeQuery(id+"F0.imprint","IMPRINT",EDGE,{"derivedFrom":sQuery(id+"F0.wireOp",EDGE,"E16.0")}),1.0]])]});
            var Q38;
            Q38=makeQuery(id+"F0.imprint","IMPRINT",FACE,{"disambiguationData":[TD([[makeQuery(id+"F0.imprint","IMPRINT",EDGE,{"derivedFrom":sQuery(id+"F0.wireOp",EDGE,"E12.0")}),1.0]])]});
            var Q39;
            Q39=makeQuery(id+"F0.imprint","IMPRINT",FACE,{"disambiguationData":[TD([[makeQuery(id+"F0.imprint","IMPRINT",EDGE,{"derivedFrom":sQuery(id+"F0.wireOp",EDGE,"E6.0")}),1.0]])]});
            var Q40;
            Q40=makeQuery(id+"F0.imprint","IMPRINT",FACE,{"disambiguationData":[TD([[makeQuery(id+"F0.imprint","IMPRINT",EDGE,{"derivedFrom":sQuery(id+"F0.wireOp",EDGE,"E8.0")}),1.0]])]});
            var Q41;
            Q41=makeQuery(id+"F0.imprint","IMPRINT",FACE,{"disambiguationData":[TD([[makeQuery(id+"F0.imprint","IMPRINT",EDGE,{"derivedFrom":sQuery(id+"F0.wireOp",EDGE,"E26.0")}),1.0]])]});
            var Q42;
            Q42=makeQuery(id+"F0.imprint","IMPRINT",FACE,{"disambiguationData":[TD([[makeQuery(id+"F0.imprint","IMPRINT",EDGE,{"derivedFrom":sQuery(id+"F0.wireOp",EDGE,"E4.0")}),1.0]])]});
            extrude(context, id + "F1", {"entities" : qUnion([Q0, Q1, Q2, Q3, Q4, Q5, Q6, Q7, Q8, Q9, Q10, Q11, Q12, Q13, Q14, Q15, Q16, Q17, Q18, Q19, Q20, Q21, Q22, Q23, Q24, Q25, Q26, Q27, Q28, Q29, Q30, Q31, Q32, Q33, Q34, Q35, Q36, Q37, Q38, Q39, Q40, Q41, Q42]), "oppositeDirection" : true, "depth" : 30 * mm, "offsetDistance" : 25 * mm});
        }
        {
            var Q0;
            Q0=qCreatedBy(makeId("Top.planeOp"),FACE);
            var sketch = newSketch(context, id + "F2", { "sketchPlane" : qUnion([Q0])});
            skCircle(sketch, "E30", {"center": v(0, 0) * mm, "radius": 8 * mm});
            skSolve(sketch);
        }
        {
            var Q0;
            Q0=makeQuery(id+"F2.imprint","IMPRINT",FACE,{"disambiguationData":[TD([[makeQuery(id+"F2.imprint","IMPRINT",EDGE,{"derivedFrom":sQuery(id+"F2.wireOp",EDGE,"E30")}),1.0]])]});
            extrude(context, id + "F3", {"entities" : qUnion([Q0]), "operationType" : NewBodyOperationType.REMOVE, "oppositeDirection" : true, "depth" : 12 * mm, "offsetDistance" : 25 * mm});
        }
    });
